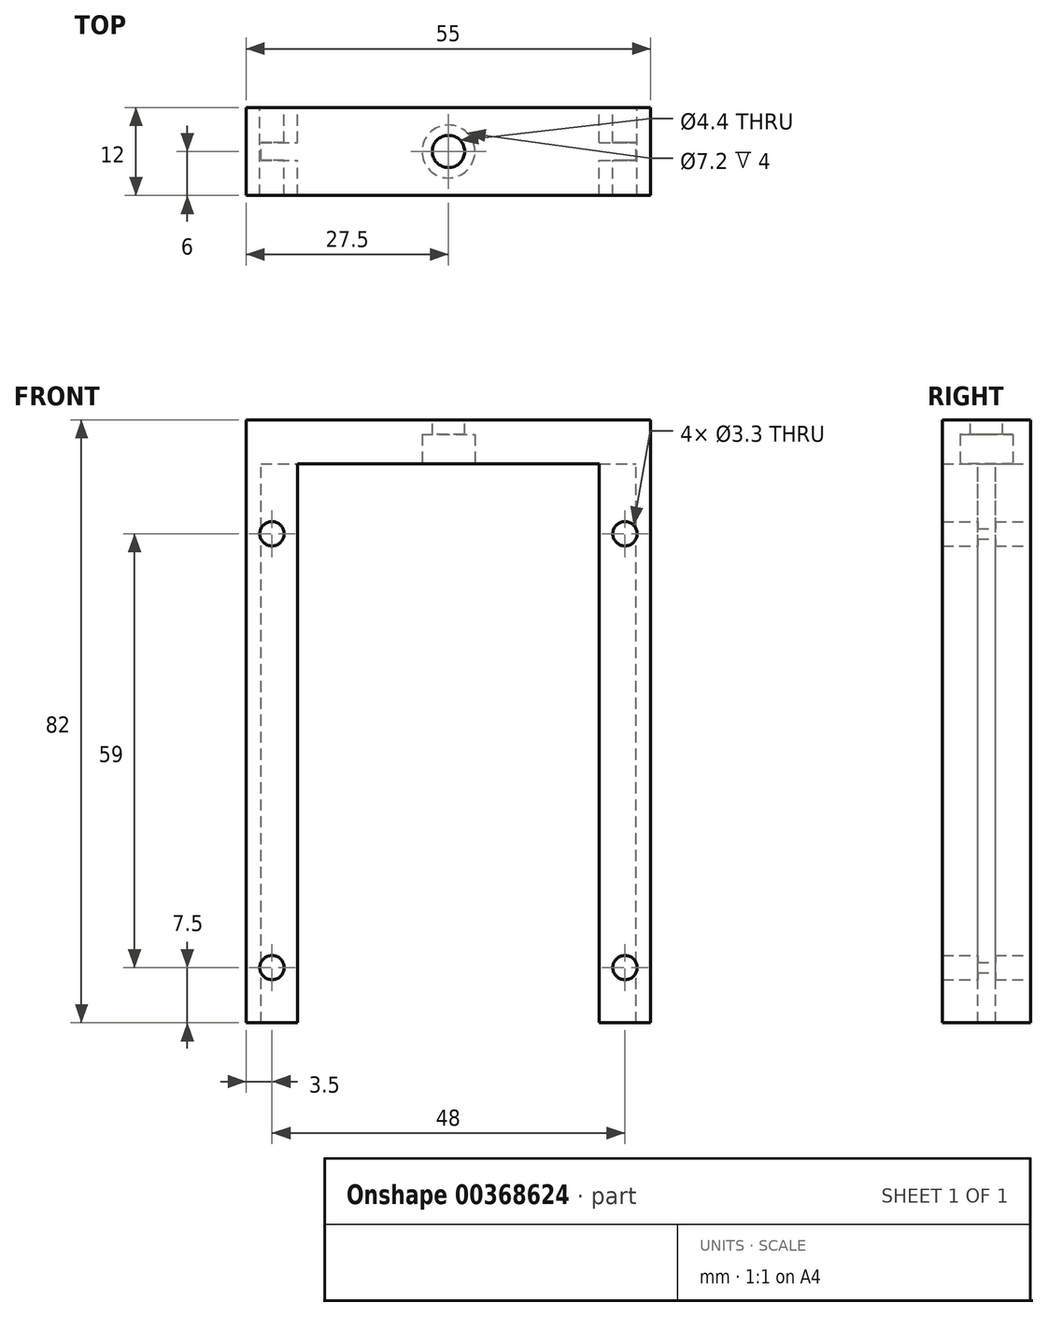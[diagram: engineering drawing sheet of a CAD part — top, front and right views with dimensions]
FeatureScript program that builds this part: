
annotation { "Feature Type Name" : "Feature", "Feature Type Description" : "" }
export const myFeature = defineFeature(function(context is Context, id is Id, definition is map)
    precondition{}
    {
        {
            var Q0;
            Q0=qCreatedBy(makeId("Top.planeOp"),FACE);
            var sketch = newSketch(context, id + "F0", { "sketchPlane" : qUnion([Q0])});
            skLineSegment(sketch, "E0.bottom", {"start": v(27.5, 6) * mm, "end": v(-27.5, 6) * mm});
            skLineSegment(sketch, "E0.top", {"start": v(27.5, -6) * mm, "end": v(-27.5, -6) * mm});
            skLineSegment(sketch, "E0.left", {"start": v(27.5, 6) * mm, "end": v(27.5, -6) * mm});
            skLineSegment(sketch, "E0.right", {"start": v(-27.5, 6) * mm, "end": v(-27.5, -6) * mm});
            skPoint(sketch, "E0.middle", {"position": v(0, 0) * mm});
            skSolve(sketch);
        }
        {
            var Q0;
            Q0=makeQuery(id+"F0.imprint","IMPRINT",FACE,{"disambiguationData":[TD([[makeQuery(id+"F0.imprint","IMPRINT",EDGE,{"derivedFrom":sQuery(id+"F0.wireOp",EDGE,"E0.bottom")}),1.0]])]});
            extrude(context, id + "F1", {"entities" : qUnion([Q0]), "oppositeDirection" : true, "depth" : 6 * mm});
        }
        {
            var Q0;
            Q0=sQuery(id+"F0.wireOp",VERTEX,"E0.middle");
            var Q1;
            Q1=makeQuery(id+"F1.opExtrude","SWEPT_BODY",BODY,{"disambiguationData":[OSD([sQuery(id+"F0.wireOp",EDGE,"E0.bottom"),sQuery(id+"F0.wireOp",EDGE,"E0.top"),sQuery(id+"F0.wireOp",EDGE,"E0.left"),sQuery(id+"F0.wireOp",EDGE,"E0.right")])]});
            hole(context, id + "F2", {"style" : HoleStyle.SIMPLE, "endStyle" : HoleEndStyle.THROUGH, "standardTappedOrClearance" : lookupTablePath({ "standard" : "ISO", "fit" : "Normal", "size" : "M4", "type" : "Clearance" }), "standardBlindInLast" : lookupTablePath({ "fit" : "Standard", "standard" : "ISO", "size" : "M4", "type" : "Clearance" }), "holeDiameter" : 4.4 * mm, "isTappedThrough" : true, "tappedDepth" : 12 * mm, "tapClearance" : 3, "startFromSketch" : true, "locations" : qUnion([Q0]), "scope" : qUnion([Q1])});
        }
        {
            var Q0;
            Q0=makeQuery(id+"F1.opExtrude","CAP_FACE",FACE,{"disambiguationData":[OSD([sQuery(id+"F0.wireOp",EDGE,"E0.bottom"),sQuery(id+"F0.wireOp",EDGE,"E0.top"),sQuery(id+"F0.wireOp",EDGE,"E0.left"),sQuery(id+"F0.wireOp",EDGE,"E0.right")])],"isStart":false});
            var sketch = newSketch(context, id + "F3", { "sketchPlane" : qUnion([Q0])});
            skLineSegment(sketch, "E1.bottom", {"start": v(-27.5, 6) * mm, "end": v(27.5, 6) * mm, "construction": true});
            skLineSegment(sketch, "E1.top", {"start": v(-27.5, -6) * mm, "end": v(27.5, -6) * mm, "construction": true});
            skLineSegment(sketch, "E1.left", {"start": v(-27.5, 6) * mm, "end": v(-27.5, -6) * mm, "construction": true});
            skLineSegment(sketch, "E1.right", {"start": v(27.5, 6) * mm, "end": v(27.5, -6) * mm, "construction": true});
            skPoint(sketch, "E1.middle", {"position": v(0, 0) * mm});
            skLineSegment(sketch, "E2.bottom", {"start": v(-27.5, 6) * mm, "end": v(-20.5, 6) * mm});
            skLineSegment(sketch, "E2.top", {"start": v(-27.5, -6) * mm, "end": v(-20.5, -6) * mm});
            skLineSegment(sketch, "E2.left", {"start": v(-27.5, 6) * mm, "end": v(-27.5, -6) * mm});
            skLineSegment(sketch, "E2.right", {"start": v(-20.5, 6) * mm, "end": v(-20.5, -6) * mm});
            skLineSegment(sketch, "E3.bottom", {"start": v(27.5, 6) * mm, "end": v(20.5, 6) * mm});
            skLineSegment(sketch, "E3.top", {"start": v(27.5, -6) * mm, "end": v(20.5, -6) * mm});
            skLineSegment(sketch, "E3.left", {"start": v(27.5, 6) * mm, "end": v(27.5, -6) * mm});
            skLineSegment(sketch, "E3.right", {"start": v(20.5, 6) * mm, "end": v(20.5, -6) * mm});
            skLineSegment(sketch, "E4.bottom", {"start": v(25.5, -1.2) * mm, "end": v(-25.5, -1.2) * mm, "construction": true});
            skLineSegment(sketch, "E4.top", {"start": v(25.5, 1.2) * mm, "end": v(-25.5, 1.2) * mm, "construction": true});
            skLineSegment(sketch, "E4.left", {"start": v(25.5, -1.2) * mm, "end": v(25.5, 1.2) * mm, "construction": true});
            skLineSegment(sketch, "E4.right", {"start": v(-25.5, -1.2) * mm, "end": v(-25.5, 1.2) * mm, "construction": true});
            skLineSegment(sketch, "E5.bottom", {"start": v(-25.5, 1.2) * mm, "end": v(-20.5, 1.2) * mm});
            skLineSegment(sketch, "E5.top", {"start": v(-25.5, -1.2) * mm, "end": v(-20.5, -1.2) * mm});
            skLineSegment(sketch, "E5.left", {"start": v(-25.5, 1.2) * mm, "end": v(-25.5, -1.2) * mm});
            skLineSegment(sketch, "E5.right", {"start": v(-20.5, 1.2) * mm, "end": v(-20.5, -1.2) * mm});
            skLineSegment(sketch, "E6.bottom", {"start": v(20.5, 1.2) * mm, "end": v(25.5, 1.2) * mm});
            skLineSegment(sketch, "E6.top", {"start": v(20.5, -1.2) * mm, "end": v(25.5, -1.2) * mm});
            skLineSegment(sketch, "E6.left", {"start": v(20.5, 1.2) * mm, "end": v(20.5, -1.2) * mm});
            skLineSegment(sketch, "E6.right", {"start": v(25.5, 1.2) * mm, "end": v(25.5, -1.2) * mm});
            skSolve(sketch);
        }
        {
            var Q0;
            {var subQ1=sQuery(id+"F3.wireOp",EDGE,"E2.bottom");Q0=makeQuery(id+"F3.imprint","IMPRINT",FACE,{"disambiguationData":[TD([[makeQuery(id+"F3.imprint","IMPRINT",EDGE,{"derivedFrom":subQ1}),1.0]])]});}
            var Q1;
            {var subQ1=sQuery(id+"F3.wireOp",EDGE,"E3.bottom");Q1=makeQuery(id+"F3.imprint","IMPRINT",FACE,{"disambiguationData":[TD([[makeQuery(id+"F3.imprint","IMPRINT",EDGE,{"derivedFrom":subQ1}),1.0]])]});}
            extrude(context, id + "F4", {"entities" : qUnion([Q0, Q1]), "operationType" : NewBodyOperationType.ADD, "depth" : 76 * mm});
        }
        {
            var Q0;
            Q0=makeQuery(id+"F4.boolean.opBoolean","MERGE",FACE,{"derivedFrom":[makeQuery(id+"F1.opExtrude","SWEPT_FACE",FACE,{"disambiguationData":[OSD([sQuery(id+"F0.wireOp",EDGE,"E0.bottom")])]}),makeQuery(id+"F4.opExtrude","SWEPT_FACE",FACE,{"disambiguationData":[OSD([sQuery(id+"F3.wireOp",EDGE,"E2.top")])]}),makeQuery(id+"F4.opExtrude","SWEPT_FACE",FACE,{"disambiguationData":[OSD([sQuery(id+"F3.wireOp",EDGE,"E3.top")])]})]});
            var sketch = newSketch(context, id + "F5", { "sketchPlane" : qUnion([Q0])});
            skLineSegment(sketch, "E7", {"start": v(24, -82) * mm, "end": v(24, 0) * mm, "construction": true});
            skPoint(sketch, "E8", {"position": v(24, -74.5) * mm});
            skPoint(sketch, "E9", {"position": v(24, -15.5) * mm});
            skLineSegment(sketch, "E10", {"start": v(-24, -82) * mm, "end": v(-24, 0) * mm, "construction": true});
            skPoint(sketch, "E11", {"position": v(-24, -74.5) * mm});
            skPoint(sketch, "E12", {"position": v(-24, -15.5) * mm});
            skSolve(sketch);
        }
        {
            var Q0;
            Q0=sQuery(id+"F5.wireOp",VERTEX,"E8");
            var Q1;
            Q1=makeQuery(id+"F1.opExtrude","SWEPT_BODY",BODY,{"disambiguationData":[OSD([sQuery(id+"F0.wireOp",EDGE,"E0.bottom"),sQuery(id+"F0.wireOp",EDGE,"E0.top"),sQuery(id+"F0.wireOp",EDGE,"E0.left"),sQuery(id+"F0.wireOp",EDGE,"E0.right")])]});
            hole(context, id + "F6", {"style" : HoleStyle.SIMPLE, "endStyle" : HoleEndStyle.THROUGH, "standardTappedOrClearance" : lookupTablePath({ "standard" : "ISO", "fit" : "Normal", "size" : "M3", "type" : "Clearance" }), "standardBlindInLast" : lookupTablePath({ "fit" : "Standard", "standard" : "ISO", "size" : "M3", "type" : "Clearance" }), "holeDiameter" : 3.3 * mm, "isTappedThrough" : true, "tappedDepth" : 12 * mm, "tapClearance" : 3, "startFromSketch" : true, "locations" : qUnion([Q0]), "scope" : qUnion([Q1])});
        }
        {
            var Q0;
            Q0=sQuery(id+"F5.wireOp",VERTEX,"E11");
            var Q1;
            Q1=makeQuery(id+"F1.opExtrude","SWEPT_BODY",BODY,{"disambiguationData":[OSD([sQuery(id+"F0.wireOp",EDGE,"E0.bottom"),sQuery(id+"F0.wireOp",EDGE,"E0.top"),sQuery(id+"F0.wireOp",EDGE,"E0.left"),sQuery(id+"F0.wireOp",EDGE,"E0.right")])]});
            hole(context, id + "F7", {"style" : HoleStyle.SIMPLE, "endStyle" : HoleEndStyle.THROUGH, "standardTappedOrClearance" : lookupTablePath({ "standard" : "ISO", "fit" : "Normal", "size" : "M3", "type" : "Clearance" }), "standardBlindInLast" : lookupTablePath({ "fit" : "Standard", "standard" : "ISO", "size" : "M3", "type" : "Clearance" }), "holeDiameter" : 3.3 * mm, "isTappedThrough" : true, "tappedDepth" : 12 * mm, "tapClearance" : 3, "startFromSketch" : true, "locations" : qUnion([Q0]), "scope" : qUnion([Q1])});
        }
        {
            var Q0;
            Q0=sQuery(id+"F5.wireOp",VERTEX,"E9");
            var Q1;
            Q1=makeQuery(id+"F1.opExtrude","SWEPT_BODY",BODY,{"disambiguationData":[OSD([sQuery(id+"F0.wireOp",EDGE,"E0.bottom"),sQuery(id+"F0.wireOp",EDGE,"E0.top"),sQuery(id+"F0.wireOp",EDGE,"E0.left"),sQuery(id+"F0.wireOp",EDGE,"E0.right")])]});
            hole(context, id + "F8", {"style" : HoleStyle.SIMPLE, "endStyle" : HoleEndStyle.THROUGH, "standardTappedOrClearance" : lookupTablePath({ "standard" : "ISO", "fit" : "Normal", "size" : "M3", "type" : "Clearance" }), "standardBlindInLast" : lookupTablePath({ "fit" : "Standard", "standard" : "ISO", "size" : "M3", "type" : "Clearance" }), "holeDiameter" : 3.3 * mm, "isTappedThrough" : true, "tappedDepth" : 12 * mm, "tapClearance" : 3, "startFromSketch" : true, "locations" : qUnion([Q0]), "scope" : qUnion([Q1])});
        }
        {
            var Q0;
            Q0=sQuery(id+"F5.wireOp",VERTEX,"E12");
            var Q1;
            Q1=makeQuery(id+"F1.opExtrude","SWEPT_BODY",BODY,{"disambiguationData":[OSD([sQuery(id+"F0.wireOp",EDGE,"E0.bottom"),sQuery(id+"F0.wireOp",EDGE,"E0.top"),sQuery(id+"F0.wireOp",EDGE,"E0.left"),sQuery(id+"F0.wireOp",EDGE,"E0.right")])]});
            hole(context, id + "F9", {"style" : HoleStyle.SIMPLE, "endStyle" : HoleEndStyle.THROUGH, "standardTappedOrClearance" : lookupTablePath({ "standard" : "ISO", "fit" : "Normal", "size" : "M3", "type" : "Clearance" }), "standardBlindInLast" : lookupTablePath({ "fit" : "Standard", "standard" : "ISO", "size" : "M3", "type" : "Clearance" }), "holeDiameter" : 3.3 * mm, "isTappedThrough" : true, "tappedDepth" : 12 * mm, "tapClearance" : 3, "startFromSketch" : true, "locations" : qUnion([Q0]), "scope" : qUnion([Q1])});
        }
        {
            var Q0;
            Q0=makeQuery(id+"F1.opExtrude","CAP_FACE",FACE,{"disambiguationData":[OSD([sQuery(id+"F0.wireOp",EDGE,"E0.bottom"),sQuery(id+"F0.wireOp",EDGE,"E0.top"),sQuery(id+"F0.wireOp",EDGE,"E0.left"),sQuery(id+"F0.wireOp",EDGE,"E0.right")])],"isStart":false});
            var sketch = newSketch(context, id + "F10", { "sketchPlane" : qUnion([Q0])});
            skCircle(sketch, "E13", {"center": v(0, 0) * mm, "radius": 2.2 * mm});
            skCircle(sketch, "E14", {"center": v(0, 0) * mm, "radius": 3.6 * mm});
            skSolve(sketch);
        }
        {
            var Q0;
            Q0=makeQuery(id+"F10.imprint","IMPRINT",FACE,{"disambiguationData":[TD([[makeQuery(id+"F10.imprint","IMPRINT",EDGE,{"derivedFrom":sQuery(id+"F10.wireOp",EDGE,"E13")}),-1.0]])]});
            extrude(context, id + "F11", {"entities" : qUnion([Q0]), "operationType" : NewBodyOperationType.REMOVE, "oppositeDirection" : true, "depth" : 4 * mm});
        }
    });
